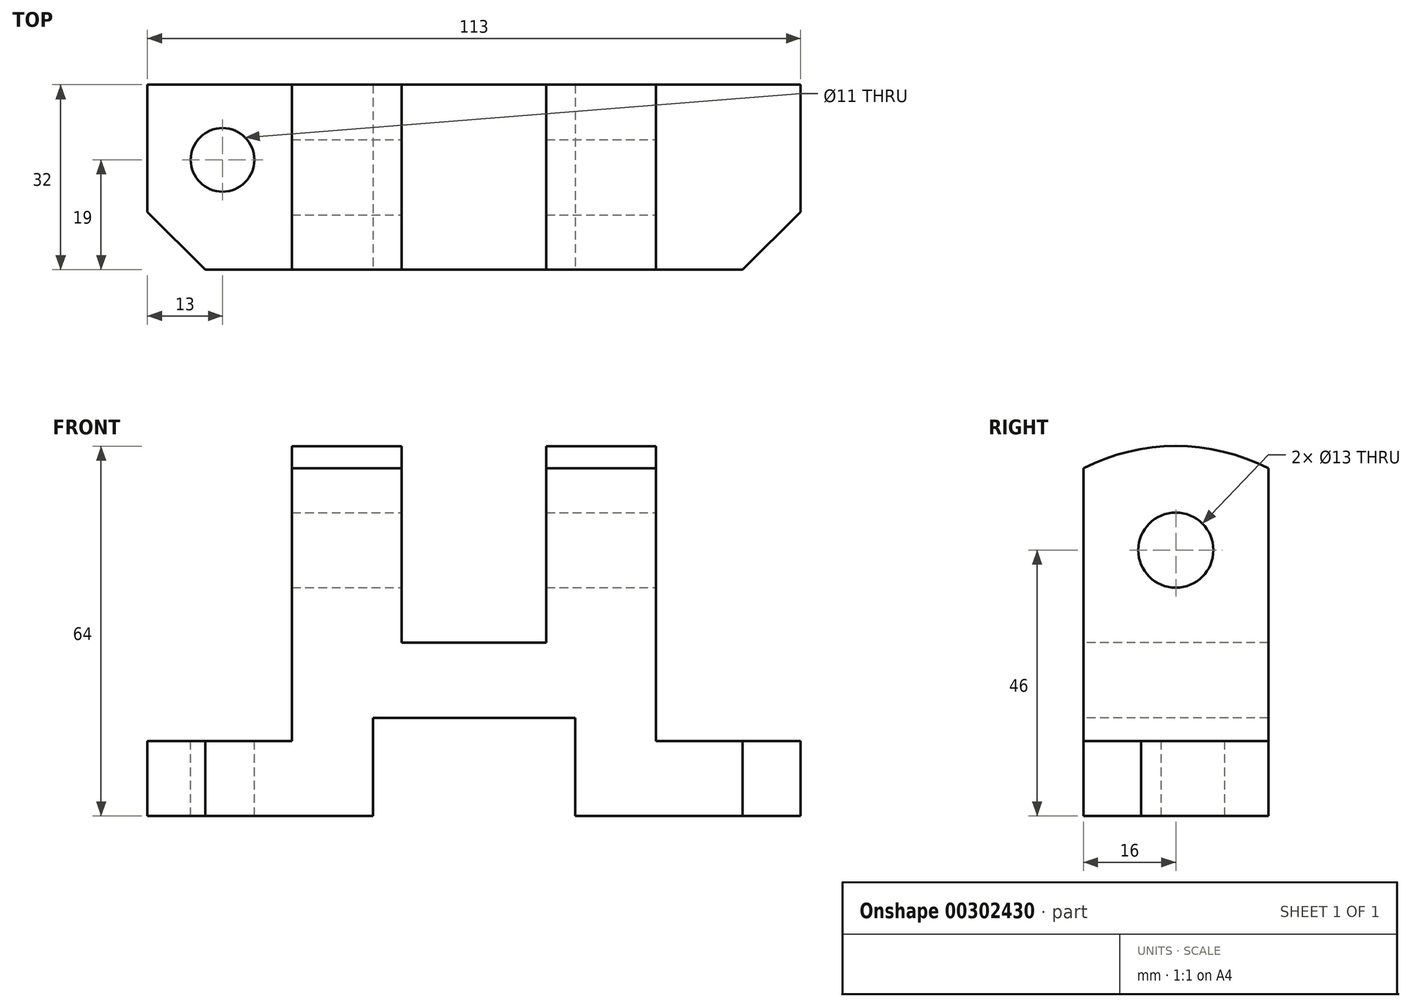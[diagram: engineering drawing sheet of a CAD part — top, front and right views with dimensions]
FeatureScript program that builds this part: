
annotation { "Feature Type Name" : "Feature", "Feature Type Description" : "" }
export const myFeature = defineFeature(function(context is Context, id is Id, definition is map)
    precondition{}
    {
        {
            var Q0;
            Q0=qCreatedBy(makeId("Right.planeOp"),FACE);
            var sketch = newSketch(context, id + "F0", { "sketchPlane" : qUnion([Q0])});
            skLineSegment(sketch, "E0.top", {"start": v(16, 0) * mm, "end": v(-16, 0) * mm});
            skLineSegment(sketch, "E0.left", {"start": v(16, 60.13) * mm, "end": v(16, 0) * mm});
            skLineSegment(sketch, "E0.right", {"start": v(-16, 60.13) * mm, "end": v(-16, 0) * mm});
            skArc(sketch, "E1", {"start": v(16, 60.13) * mm, "mid": v(0, 64) * mm, "end": v(-16, 60.13) * mm});
            skSolve(sketch);
        }
        {
            var Q0;
            Q0 = qSketchRegion(id + "F0", true);
            extrude(context, id + "F1", {"entities" : qUnion([Q0]), "depth" : 113 * mm});
        }
        {
            var Q0;
            Q0=makeQuery(id+"F1.opExtrude","SWEPT_FACE",FACE,{"disambiguationData":[OSD([sQuery(id+"F0.wireOp",EDGE,"E0.right")])]});
            var sketch = newSketch(context, id + "F2", { "sketchPlane" : qUnion([Q0])});
            skLineSegment(sketch, "E2.bottom", {"start": v(44, 181.75) * mm, "end": v(69, 181.75) * mm});
            skLineSegment(sketch, "E2.top", {"start": v(44, 30) * mm, "end": v(69, 30) * mm});
            skLineSegment(sketch, "E2.left", {"start": v(44, 181.75) * mm, "end": v(44, 30) * mm});
            skLineSegment(sketch, "E2.right", {"start": v(69, 181.75) * mm, "end": v(69, 30) * mm});
            skLineSegment(sketch, "E3.bottom", {"start": v(88, 138.7) * mm, "end": v(113, 138.7) * mm});
            skLineSegment(sketch, "E3.top", {"start": v(88, 13) * mm, "end": v(113, 13) * mm});
            skLineSegment(sketch, "E3.left", {"start": v(88, 138.7) * mm, "end": v(88, 13) * mm});
            skLineSegment(sketch, "E3.right", {"start": v(113, 138.7) * mm, "end": v(113, 13) * mm});
            skLineSegment(sketch, "E4", {"start": v(56.5, 157.93) * mm, "end": v(56.5, -30.46) * mm, "construction": true});
            skPoint(sketch, "E4.startSnap0", {"position": v(56.5, 181.75) * mm});
            skLineSegment(sketch, "E5.MirrorCS", {"start": v(25, 138.7) * mm, "end": v(25, 13) * mm});
            skLineSegment(sketch, "E6.MirrorCS", {"start": v(25, 138.7) * mm, "end": v(0, 138.7) * mm});
            skLineSegment(sketch, "E7.MirrorCS", {"start": v(0, 138.7) * mm, "end": v(0, 13) * mm});
            skLineSegment(sketch, "E8.MirrorCS", {"start": v(25, 13) * mm, "end": v(0, 13) * mm});
            skLineSegment(sketch, "E9.bottom", {"start": v(39, 17) * mm, "end": v(74, 17) * mm});
            skLineSegment(sketch, "E9.top", {"start": v(39, 0) * mm, "end": v(74, 0) * mm});
            skLineSegment(sketch, "E9.left", {"start": v(39, 17) * mm, "end": v(39, 0) * mm});
            skLineSegment(sketch, "E9.right", {"start": v(74, 17) * mm, "end": v(74, 0) * mm});
            skSolve(sketch);
        }
        {
            var Q0;
            Q0 = qSketchRegion(id + "F2", true);
            extrude(context, id + "F3", {"entities" : qUnion([Q0]), "operationType" : NewBodyOperationType.REMOVE, "endBound" : BoundingType.THROUGH_ALL, "oppositeDirection" : true, "depth" : 25 * mm});
        }
        {
            var Q0;
            Q0=makeQuery(id+"F1.opExtrude","CAP_EDGE",EDGE,{"disambiguationData":[OSD([sQuery(id+"F0.wireOp",EDGE,"E0.right")])],"isStart":true});
            var Q1;
            Q1=makeQuery(id+"F1.opExtrude","CAP_EDGE",EDGE,{"disambiguationData":[OSD([sQuery(id+"F0.wireOp",EDGE,"E0.right")])],"isStart":false});
            chamfer(context, id + "F4", {"entities" : qUnion([Q0, Q1]), "width" : 10 * mm, "tangentPropagation" : true});
        }
        {
            var Q0;
            Q0=makeQuery(id+"F3.boolean.opBoolean","COPY",FACE,{"derivedFrom":makeQuery(id+"F3.opExtrude","SWEPT_FACE",FACE,{"disambiguationData":[OSD([sQuery(id+"F2.wireOp",EDGE,"E8.MirrorCS")])]})});
            var sketch = newSketch(context, id + "F5", { "sketchPlane" : qUnion([Q0])});
            skCircle(sketch, "E10", {"center": v(13, 3) * mm, "radius": 5.5 * mm});
            skLineSegment(sketch, "E11", {"start": v(56.5, 22.34) * mm, "end": v(56.5, -21.26) * mm, "construction": true});
            skCircle(sketch, "E12.MirrorC", {"center": v(100, 3) * mm, "radius": 5.5 * mm});
            skSolve(sketch);
        }
        {
            var Q0;
            Q0=makeQuery(id+"F5.imprint","IMPRINT",FACE,{"disambiguationData":[TD([[makeQuery(id+"F5.imprint","IMPRINT",EDGE,{"derivedFrom":sQuery(id+"F5.wireOp",EDGE,"E12.MirrorC")}),-1.0]])]});
            var Q1;
            Q1=makeQuery(id+"F5.imprint","IMPRINT",FACE,{"disambiguationData":[TD([[makeQuery(id+"F5.imprint","IMPRINT",EDGE,{"derivedFrom":sQuery(id+"F5.wireOp",EDGE,"E10")}),1.0]])]});
            extrude(context, id + "F6", {"entities" : qUnion([Q0, Q1]), "operationType" : NewBodyOperationType.REMOVE, "oppositeDirection" : true, "depth" : 25 * mm});
        }
        {
            var Q0;
            Q0=makeQuery(id+"F3.boolean.opBoolean","COPY",FACE,{"derivedFrom":makeQuery(id+"F3.opExtrude","SWEPT_FACE",FACE,{"disambiguationData":[OSD([sQuery(id+"F2.wireOp",EDGE,"E3.left")])]})});
            var sketch = newSketch(context, id + "F7", { "sketchPlane" : qUnion([Q0])});
            skCircle(sketch, "E13", {"center": v(0, 46) * mm, "radius": 6.5 * mm});
            skSolve(sketch);
        }
        {
            var Q0;
            Q0 = qSketchRegion(id + "F7", true);
            extrude(context, id + "F8", {"entities" : qUnion([Q0]), "operationType" : NewBodyOperationType.REMOVE, "endBound" : BoundingType.THROUGH_ALL, "oppositeDirection" : true, "depth" : 25 * mm});
        }
    });
